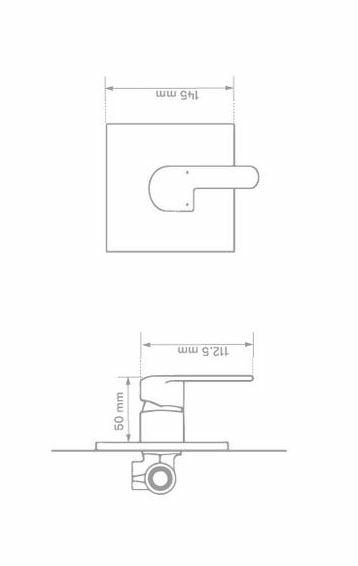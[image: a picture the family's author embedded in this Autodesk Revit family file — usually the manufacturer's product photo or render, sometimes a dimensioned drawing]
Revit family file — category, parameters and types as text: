
# Revit family: 01-1535-11SR-MEZCLADOR DUCHA 8 SST PIANA
name_source: partatom
category: Aparatos sanitarios
revit_build: Autodesk Revit 2018 (Build: 20170223_1515(x64)
units: mm (PartAtom-declared; Revit-internal decimal feet)

## family parameters
Anfitrión = Cara
Compartido = No
Corte con vacíos al cargar = No
Cota de conector redondo = Diámetro de uso
Número OmniClass = 23.31.11.00
Punto de cálculo de habitación = No
Tipo de pieza = Normal

## types (1)
- 01-1535-11SR
    Alto = 75 mm
    Ancho = 60 mm  [stored 0.19685 ft]
    Conexión AC = Sí
    Conexión AF = Sí
    Conexión de residuos = No
    Conexión de ventilación = No
    Descripción = Mezclador ducha
    Distancia entre griferias = 203 mm
    Elevación por defecto = 0 mm  [stored 0 ft]
    Fabricante = Gricol
    Finish = Cromo Gricol
    Imagen de tipo = <Ninguno>
    Link Ficha Tecnica = https://infotecnica.gricol.com
    Modelo = 01-1535-11SR
    Product Name = MEZCLADOR PIANA
    Profundidad = 85 mm  [stored 0.278871 ft]
    URL = https://www.gricol.com

note: [stored X ft] marks values corroborated as IEEE doubles in the binary element streams (Revit-internal decimal feet)

## geometry (parser evidence)
native form markers: Blend x2, Sweep x7
no freeform markers — native parametric forms only
